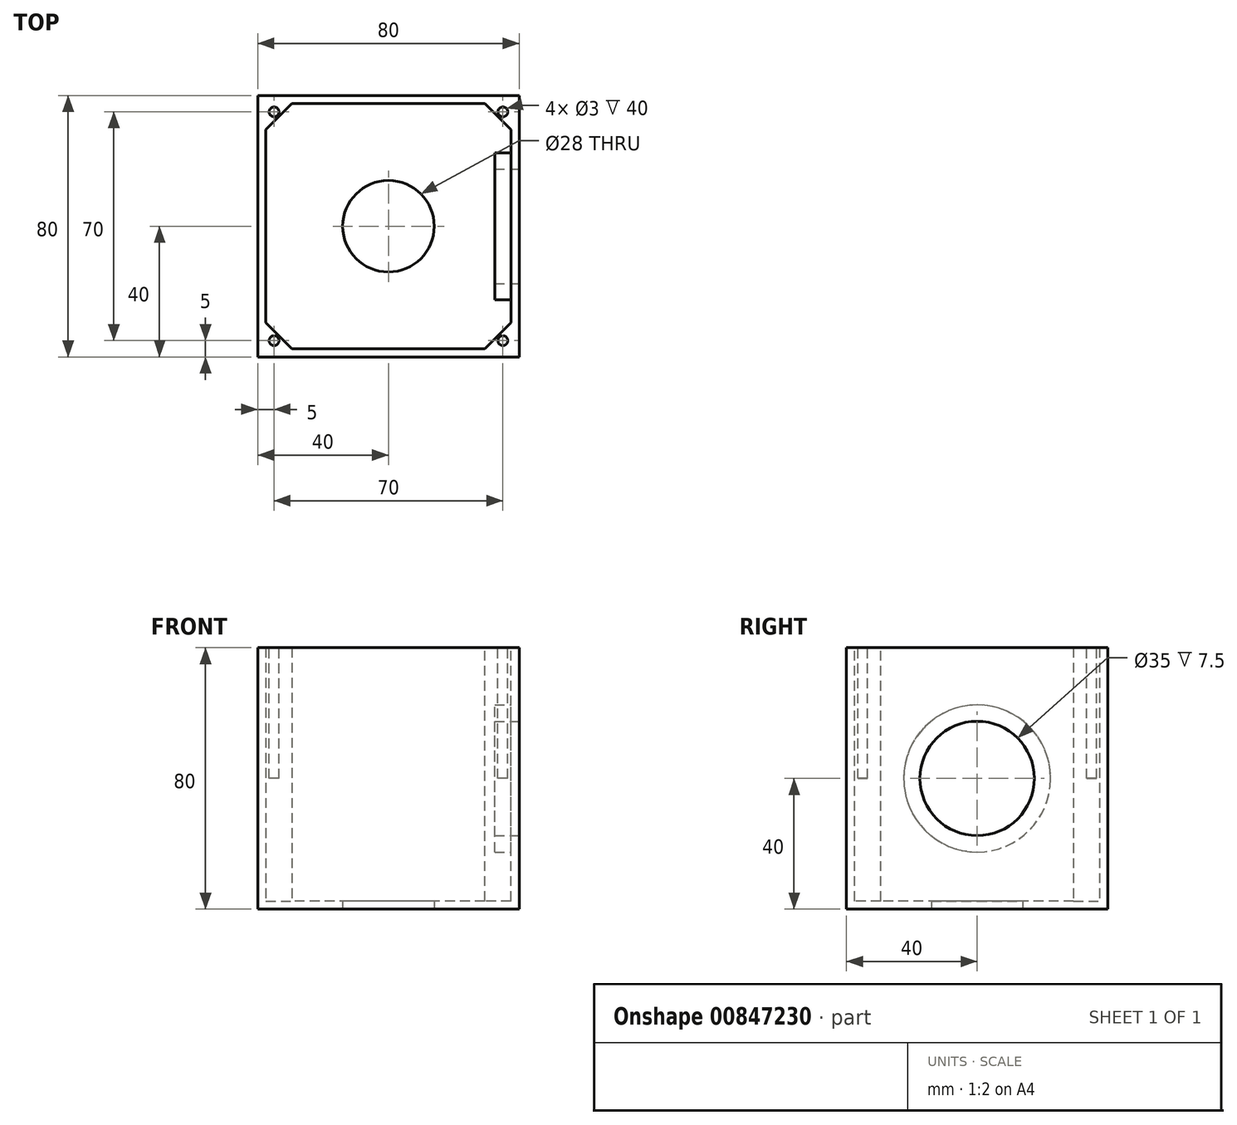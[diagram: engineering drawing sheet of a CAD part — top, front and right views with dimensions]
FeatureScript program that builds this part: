
annotation { "Feature Type Name" : "Feature", "Feature Type Description" : "" }
export const myFeature = defineFeature(function(context is Context, id is Id, definition is map)
    precondition{}
    {
        {
            var Q0;
            Q0=qCreatedBy(makeId("Top.planeOp"),FACE);
            var sketch = newSketch(context, id + "F0", { "sketchPlane" : qUnion([Q0])});
            skLineSegment(sketch, "E0.bottom", {"start": v(40, 40) * mm, "end": v(-40, 40) * mm});
            skLineSegment(sketch, "E0.top", {"start": v(40, -40) * mm, "end": v(-40, -40) * mm});
            skLineSegment(sketch, "E0.left", {"start": v(40, 40) * mm, "end": v(40, -40) * mm});
            skLineSegment(sketch, "E0.right", {"start": v(-40, 40) * mm, "end": v(-40, -40) * mm});
            skPoint(sketch, "E0.middle", {"position": v(0, 0) * mm});
            skCircle(sketch, "E1", {"center": v(0, 0) * mm, "radius": 14 * mm});
            skSolve(sketch);
        }
        {
            var Q0;
            Q0=makeQuery(id+"F0.imprint","IMPRINT",FACE,{"disambiguationData":[TD([[makeQuery(id+"F0.imprint","IMPRINT",EDGE,{"derivedFrom":sQuery(id+"F0.wireOp",EDGE,"E0.bottom")}),1.0]])]});
            var Q1;
            Q1=makeQuery(id+"F0.imprint","IMPRINT",FACE,{"disambiguationData":[TD([[makeQuery(id+"F0.imprint","IMPRINT",EDGE,{"derivedFrom":sQuery(id+"F0.wireOp",EDGE,"E1")}),1.0]])]});
            extrude(context, id + "F1", {"entities" : qUnion([Q0, Q1]), "depth" : 80 * mm, "offsetDistance" : 25 * mm});
        }
        {
            var Q0;
            Q0=makeQuery(id+"F1.opExtrude","CAP_FACE",FACE,{"disambiguationData":[OSD([sQuery(id+"F0.wireOp",EDGE,"E0.bottom"),sQuery(id+"F0.wireOp",EDGE,"E0.top"),sQuery(id+"F0.wireOp",EDGE,"E0.left"),sQuery(id+"F0.wireOp",EDGE,"E0.right"),sQuery(id+"F0.wireOp",EDGE,"E1")])],"isStart":false});
            shell(context, id + "F2", {"entities" : qUnion([Q0]), "thickness" : 2.5 * mm});
        }
        {
            var Q0;
            Q0=makeQuery(id+"F0.imprint","IMPRINT",FACE,{"disambiguationData":[TD([[makeQuery(id+"F0.imprint","IMPRINT",EDGE,{"derivedFrom":sQuery(id+"F0.wireOp",EDGE,"E1")}),1.0]])]});
            extrude(context, id + "F3", {"entities" : qUnion([Q0]), "operationType" : NewBodyOperationType.REMOVE, "endBound" : BoundingType.THROUGH_ALL, "depth" : 25 * mm, "offsetDistance" : 25 * mm});
        }
        {
            var Q0;
            Q0=makeQuery(id+"F1.opExtrude","SWEPT_FACE",FACE,{"disambiguationData":[OSD([sQuery(id+"F0.wireOp",EDGE,"E0.left")])]});
            var sketch = newSketch(context, id + "F4", { "sketchPlane" : qUnion([Q0])});
            skCircle(sketch, "E2", {"center": v(0, 40) * mm, "radius": 17.5 * mm});
            skPoint(sketch, "E2.centerSnap0", {"position": v(0, 0) * mm});
            skSolve(sketch);
        }
        {
            var Q0;
            Q0=makeQuery(id+"F4.imprint","IMPRINT",FACE,{"disambiguationData":[TD([[makeQuery(id+"F4.imprint","IMPRINT",EDGE,{"derivedFrom":sQuery(id+"F4.wireOp",EDGE,"E2")}),1.0]])]});
            extrude(context, id + "F5", {"entities" : qUnion([Q0]), "operationType" : NewBodyOperationType.REMOVE, "endBound" : BoundingType.UP_TO_NEXT, "oppositeDirection" : true, "depth" : 25 * mm, "offsetDistance" : 25 * mm});
        }
        {
            var Q0;
            Q0=makeQuery(id+"F2.opShell","OFFSET_EDGE",EDGE,{"disambiguationData":[OSD([sQuery(id+"F0.wireOp",EDGE,"E0.top"),sQuery(id+"F0.wireOp",EDGE,"E0.right")])]});
            var Q1;
            Q1=makeQuery(id+"F2.opShell","OFFSET_EDGE",EDGE,{"disambiguationData":[OSD([sQuery(id+"F0.wireOp",EDGE,"E0.bottom"),sQuery(id+"F0.wireOp",EDGE,"E0.right")])]});
            var Q2;
            Q2=makeQuery(id+"F2.opShell","OFFSET_EDGE",EDGE,{"disambiguationData":[OSD([sQuery(id+"F0.wireOp",EDGE,"E0.top"),sQuery(id+"F0.wireOp",EDGE,"E0.left")])]});
            var Q3;
            Q3=makeQuery(id+"F2.opShell","OFFSET_EDGE",EDGE,{"disambiguationData":[OSD([sQuery(id+"F0.wireOp",EDGE,"E0.bottom"),sQuery(id+"F0.wireOp",EDGE,"E0.left")])]});
            chamfer(context, id + "F6", {"entities" : qUnion([Q0, Q1, Q2, Q3]), "width" : 8 * mm, "tangentPropagation" : true});
        }
        {
            var Q0;
            Q0=makeQuery(id+"F1.opExtrude","CAP_FACE",FACE,{"disambiguationData":[OSD([sQuery(id+"F0.wireOp",EDGE,"E0.bottom"),sQuery(id+"F0.wireOp",EDGE,"E0.top"),sQuery(id+"F0.wireOp",EDGE,"E0.left"),sQuery(id+"F0.wireOp",EDGE,"E0.right")])],"isStart":false});
            var sketch = newSketch(context, id + "F7", { "sketchPlane" : qUnion([Q0])});
            skCircle(sketch, "E3", {"center": v(-35, 35) * mm, "radius": 1.5 * mm});
            skCircle(sketch, "E4.0.1.0", {"center": v(-35, -35) * mm, "radius": 1.5 * mm});
            skCircle(sketch, "E4.1.0.0", {"center": v(35, 35) * mm, "radius": 1.5 * mm});
            skCircle(sketch, "E4.1.1.0", {"center": v(35, -35) * mm, "radius": 1.5 * mm});
            skLineSegment(sketch, "E4.direction1", {"start": v(-35, 35) * mm, "end": v(35, 35) * mm, "construction": true});
            skLineSegment(sketch, "E4.direction2", {"start": v(-35, 35) * mm, "end": v(-35, -35) * mm, "construction": true});
            skSolve(sketch);
        }
        {
            var Q0;
            Q0=makeQuery(id+"F7.imprint","IMPRINT",FACE,{"disambiguationData":[TD([[makeQuery(id+"F7.imprint","IMPRINT",EDGE,{"derivedFrom":sQuery(id+"F7.wireOp",EDGE,"E4.0.1.0")}),1.0]])]});
            var Q1;
            Q1=makeQuery(id+"F7.imprint","IMPRINT",FACE,{"disambiguationData":[TD([[makeQuery(id+"F7.imprint","IMPRINT",EDGE,{"derivedFrom":sQuery(id+"F7.wireOp",EDGE,"E4.1.1.0")}),1.0]])]});
            var Q2;
            Q2=makeQuery(id+"F7.imprint","IMPRINT",FACE,{"disambiguationData":[TD([[makeQuery(id+"F7.imprint","IMPRINT",EDGE,{"derivedFrom":sQuery(id+"F7.wireOp",EDGE,"E3")}),1.0]])]});
            var Q3;
            Q3=makeQuery(id+"F7.imprint","IMPRINT",FACE,{"disambiguationData":[TD([[makeQuery(id+"F7.imprint","IMPRINT",EDGE,{"derivedFrom":sQuery(id+"F7.wireOp",EDGE,"E4.1.0.0")}),1.0]])]});
            extrude(context, id + "F8", {"entities" : qUnion([Q0, Q1, Q2, Q3]), "operationType" : NewBodyOperationType.REMOVE, "oppositeDirection" : true, "depth" : 40 * mm, "offsetDistance" : 25 * mm});
        }
        {
            var Q0;
            Q0=makeQuery(id+"F2.opShell","OFFSET_FACE",FACE,{"disambiguationData":[OSD([sQuery(id+"F0.wireOp",EDGE,"E0.left")])]});
            var sketch = newSketch(context, id + "F9", { "sketchPlane" : qUnion([Q0])});
            skCircle(sketch, "E5", {"center": v(0, 40) * mm, "radius": 22.5 * mm});
            skSolve(sketch);
        }
        {
            var Q0;
            Q0=makeQuery(id+"F9.imprint","IMPRINT",FACE,{"disambiguationData":[TD([[makeQuery(id+"F9.imprint","IMPRINT",EDGE,{"derivedFrom":sQuery(id+"F9.wireOp",EDGE,"E5")}),1.0]])]});
            var Q1;
            Q1=sQuery(id+"F9.wireOp",EDGE,"E5");
            extrude(context, id + "F10", {"entities" : qUnion([Q0]), "operationType" : NewBodyOperationType.ADD, "surfaceEntities" : qUnion([Q1]), "depth" : 5 * mm, "offsetDistance" : 25 * mm});
        }
    });
